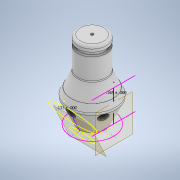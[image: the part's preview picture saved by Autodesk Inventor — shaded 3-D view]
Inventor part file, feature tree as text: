
AUTODESK INVENTOR PART (.ipt)
format: ipt  version: 2020 (Build 240168000, 168)  size: 320,512 bytes
history: native  units: in
note: dims shown in document units (in); Inventor stores cm internally (conversion verified against a paired STEP export)
features: sketch x6, hole x4, plane x2, fillet x2, revolve x1, pattern_circular x1
ambient origin geometry x8: Origin, YZ Plane, XZ Plane, XY Plane, X Axis, Y Axis, Z Axis, Center Point
bodies: Solid1 (feature_tree)
feature tree (16):
  revolve  "Revolution1"  [1 undecoded]
  hole  "Hole4"  [1 undecoded]
  hole  "Hole8"  [1 undecoded]
  sketch  "Sketch13"  dims[d2=90.0deg d3=0.057in]
  plane  "Work Plane6"
  sketch  "Sketch14"  dims[d4=0.095in d5=0.125in]
  sketch  "Sketch29"  dims[d24=0.4466in d25=0.125in]
  plane  "Work Plane5"
  sketch  "Sketch30"  dims[d54=0.3779in d72=0.3779in d83=0.75in d84=0.75in d85=0.0625in d86=0.75in d87=0.375in d88=0.25in d89=0.5635in d90=1.1in d91=0.8108in d92=0.2645in d121=0.196in d122=0.25in d123=0.375in d124=0.25in d125=0.5635in d126=0.25in d127=0.0in d137=0.3779in d155=0.3779in d173=0.3779in d191=0.3779in d221=0.3779in d239=0.3779in d253=0.4466in d254=0.1325in d255=0.0625in d256=0.25in d257=0.375in d258=0.25in d259=0.5635in d260=0.55in d261=0.0in d262=0.211in d263=0.5in d264=0.375in d265=0.25in d266=0.5635in d267=0.679in d268=0.0in d269=1.5748in d270=1.3743in d272=0.0625in d273=0.0625in]
  hole  "Hole9"  [1 undecoded]
  hole  "Hole10"  [1 undecoded]
  pattern_circular  "Circular Pattern7"  [2 undecoded]
  fillet  "Fillet1"  Radius=0.75in
  fillet  "Fillet2"  Radius=0.75in
  sketch  "Sketch12"  dims[d0=0.3328in d1=0.5in]
  sketch  "Sketch16"  dims[d6=90.0deg d23=0.65in]
note: 7 required parameter values undecoded (feature->parameter linkage not recoverable at this tier; creation-order binding heuristic only, values carry confidence <= 0.55)